# Revit family: Componenti orizzontali edificio (fare comp vert di diversa altezza)
name_source: partatom
category: Modelli generici
revit_build: Autodesk Revit 2017 (Build: 20160225_1515(x64)
units: mm (PartAtom-declared; Revit-internal decimal feet)

## family parameters
Basato su piano di lavoro = No
Condiviso = No
Punto di calcolo locali = No
Può ospitare armatura = No
Quota connettore circolare = Usa diametro
Sempre verticale = Sì
Taglio con vuoti quando caricato = No
Tipo di parte = Normale

## types (6) — shared parameters

## per-type parameters (varying)
| type | Largh 1 sx | Largh 2 Cen | Largh 3 Dx | Lungh 1 Sx | Lungh 2 Cen | Lungh 3 Dx |
| Edif_1 | 1300 mm  [stored 4.26509 ft] | 1700 mm  [stored 5.57743 ft] | 600 mm | 1600 mm  [stored 5.24934 ft] | 300 mm | 1400 mm  [stored 4.59318 ft] |
| Edif_3 | 500 mm  [stored 1.64042 ft] | 900 mm  [stored 2.95276 ft] | 2200 mm | 1340 mm  [stored 4.39633 ft] | 1700 mm  [stored 5.57743 ft] | 450 mm  [stored 1.47638 ft] |
| Edif_2 | 750 mm  [stored 2.46063 ft] | 1300 mm  [stored 4.26509 ft] | 1550 mm  [stored 5.0853 ft] | 1600 mm  [stored 5.24934 ft] | 250 mm  [stored 0.82021 ft] | 450 mm  [stored 1.47638 ft] |
| Edif_4 | 600 mm | 900 mm  [stored 2.95276 ft] | 2100 mm | 1300 mm  [stored 4.26509 ft] | 1700 mm  [stored 5.57743 ft] | 1450 mm  [stored 4.75722 ft] |
| Edif_5 | 1700 mm  [stored 5.57743 ft] | 1070 mm  [stored 3.5105 ft] | 830 mm  [stored 2.7231 ft] | 1340 mm  [stored 4.39633 ft] | 2000 mm  [stored 6.56168 ft] | 650 mm  [stored 2.13255 ft] |
| Type 6 | 1700 mm  [stored 5.57743 ft] | 1070 mm  [stored 3.5105 ft] | 830 mm  [stored 2.7231 ft] | 740 mm  [stored 2.42782 ft] | 1000 mm  [stored 3.28084 ft] | 2150 mm |

note: [stored X ft] marks values corroborated as IEEE doubles in the binary element streams (Revit-internal decimal feet)

## geometry (parser evidence)
native form markers: Sweep x3
no freeform markers — native parametric forms only
